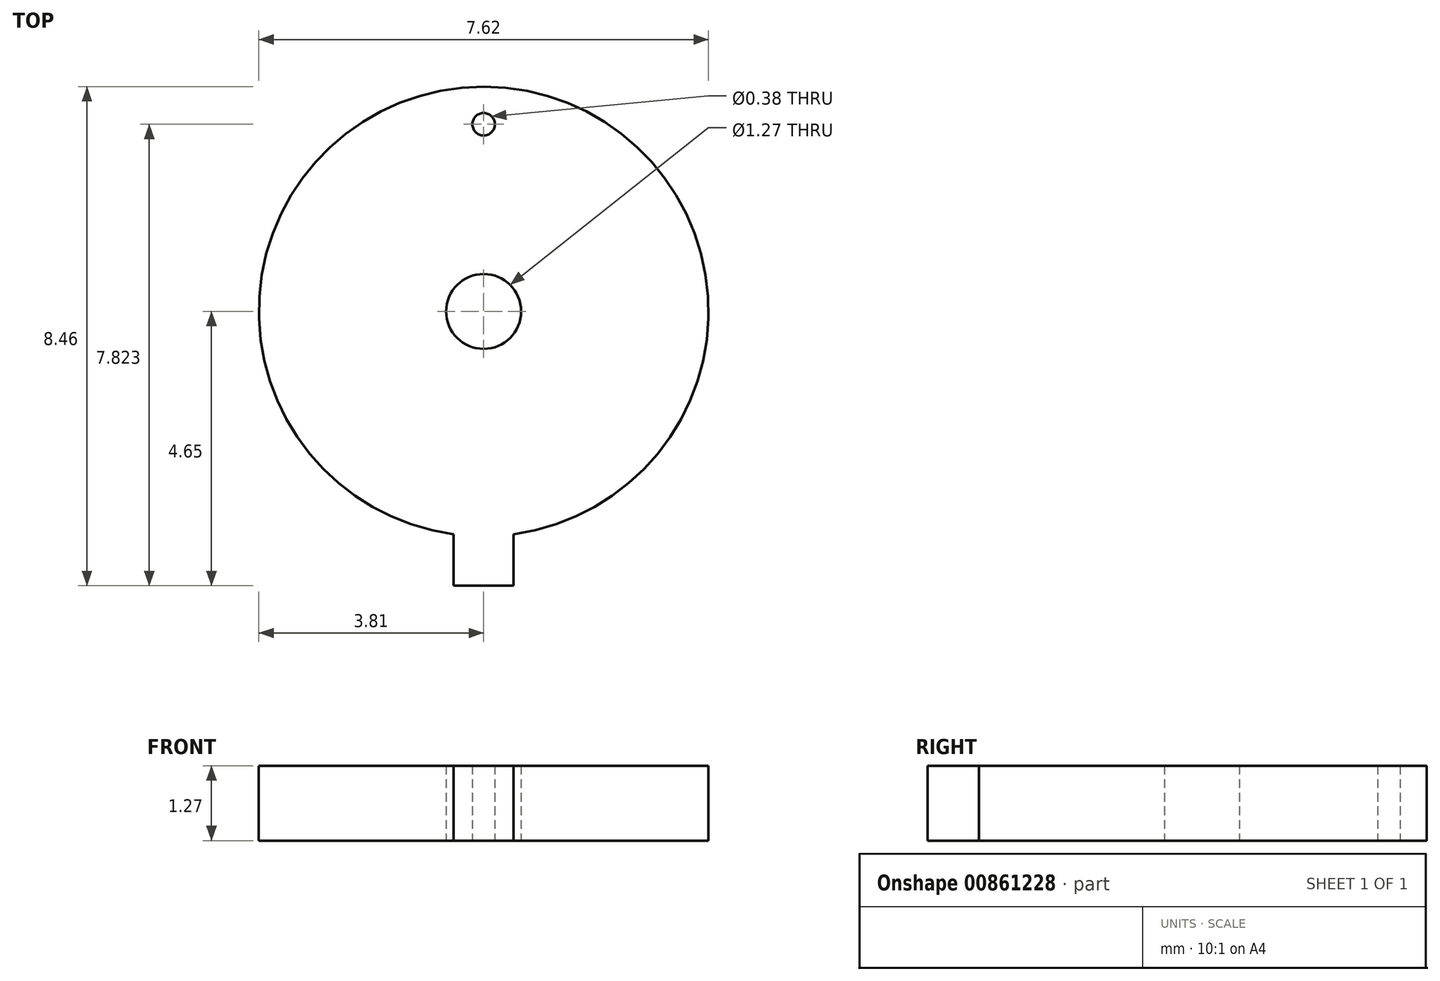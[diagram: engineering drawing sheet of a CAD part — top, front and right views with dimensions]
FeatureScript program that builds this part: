
annotation { "Feature Type Name" : "Feature", "Feature Type Description" : "" }
export const myFeature = defineFeature(function(context is Context, id is Id, definition is map)
    precondition{}
    {
        {
            var Q0;
            Q0=qCreatedBy(makeId("Top.planeOp"),FACE);
            var sketch = newSketch(context, id + "F0", { "sketchPlane" : qUnion([Q0])});
            skCircle(sketch, "E0", {"center": v(0, 0) * mm, "radius": 3.81 * mm});
            skCircle(sketch, "E1", {"center": v(0, 0) * mm, "radius": 0.64 * mm});
            skCircle(sketch, "E2", {"center": v(0, 3.17) * mm, "radius": 0.2 * mm});
            skLineSegment(sketch, "E3.bottom", {"start": v(-0.5, -2.1) * mm, "end": v(0.5, -2.1) * mm});
            skLineSegment(sketch, "E3.top", {"start": v(-0.5, -4.65) * mm, "end": v(0.5, -4.65) * mm});
            skLineSegment(sketch, "E3.left", {"start": v(-0.5, -2.1) * mm, "end": v(-0.5, -4.65) * mm});
            skLineSegment(sketch, "E3.right", {"start": v(0.5, -2.1) * mm, "end": v(0.5, -4.65) * mm});
            skSolve(sketch);
        }
        {
            var Q0;
            Q0 = qSketchRegion(id + "F0", true);
            extrude(context, id + "F1", {"entities" : qUnion([Q0]), "depth" : 1.27 * mm, "offsetDistance" : 25.4 * mm});
        }
    });
